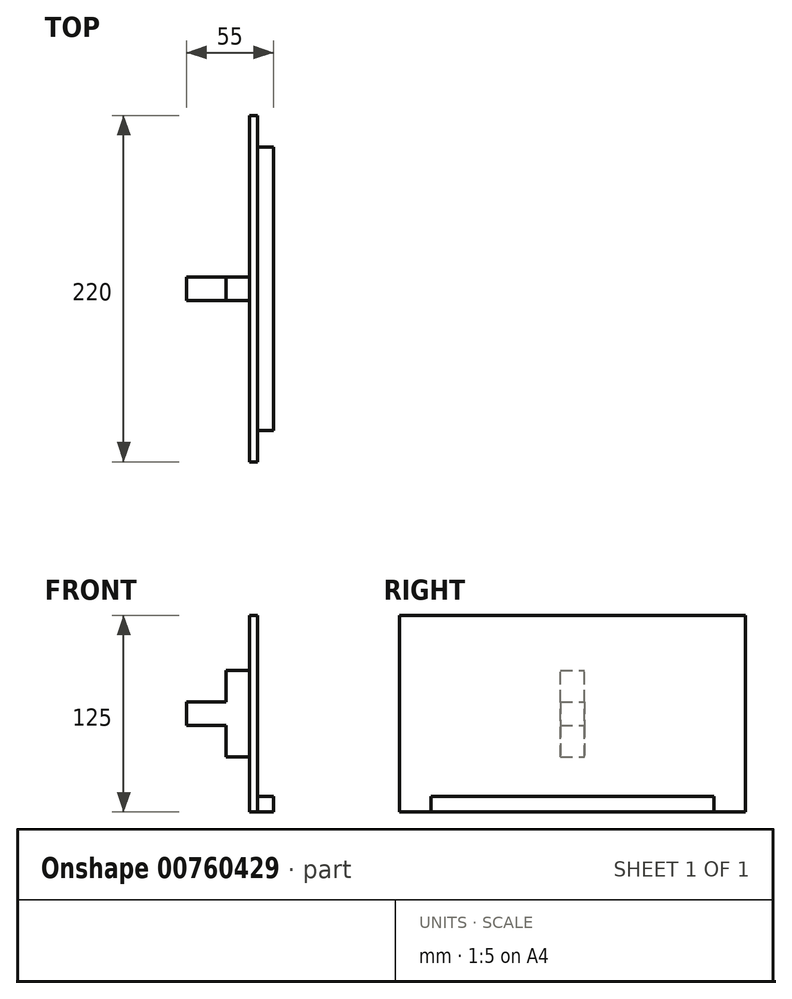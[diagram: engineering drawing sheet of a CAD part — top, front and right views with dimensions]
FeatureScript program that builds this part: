
annotation { "Feature Type Name" : "Feature", "Feature Type Description" : "" }
export const myFeature = defineFeature(function(context is Context, id is Id, definition is map)
    precondition{}
    {
        {
            var Q0;
            Q0=qCreatedBy(makeId("Front.planeOp"),FACE);
            var sketch = newSketch(context, id + "F0", { "sketchPlane" : qUnion([Q0])});
            skLineSegment(sketch, "E0.bottom", {"start": v(-20, 7.5) * mm, "end": v(20, 7.5) * mm});
            skLineSegment(sketch, "E0.top", {"start": v(-20, -7.5) * mm, "end": v(20, -7.5) * mm});
            skLineSegment(sketch, "E0.left", {"start": v(-20, 7.5) * mm, "end": v(-20, -7.5) * mm});
            skLineSegment(sketch, "E0.right", {"start": v(20, 7.5) * mm, "end": v(20, -7.5) * mm});
            skPoint(sketch, "E0.middle", {"position": v(0, 0) * mm});
            skLineSegment(sketch, "E1.bottom", {"start": v(20, 7.5) * mm, "end": v(5, 7.5) * mm});
            skLineSegment(sketch, "E1.top", {"start": v(20, 27.5) * mm, "end": v(5, 27.5) * mm});
            skLineSegment(sketch, "E1.left", {"start": v(20, 7.5) * mm, "end": v(20, 27.5) * mm});
            skLineSegment(sketch, "E1.right", {"start": v(5, 7.5) * mm, "end": v(5, 27.5) * mm});
            skLineSegment(sketch, "E2.bottom", {"start": v(20, -7.5) * mm, "end": v(5, -7.5) * mm});
            skLineSegment(sketch, "E2.top", {"start": v(20, -27.5) * mm, "end": v(5, -27.5) * mm});
            skLineSegment(sketch, "E2.left", {"start": v(20, -7.5) * mm, "end": v(20, -27.5) * mm});
            skLineSegment(sketch, "E2.right", {"start": v(5, -7.5) * mm, "end": v(5, -27.5) * mm});
            skSolve(sketch);
        }
        {
            var Q0;
            Q0=makeQuery(id+"F0.imprint","IMPRINT",FACE,{"disambiguationData":[TD([[makeQuery(id+"F0.imprint","IMPRINT",EDGE,{"derivedFrom":sQuery(id+"F0.wireOp",EDGE,"E1.top")}),1.0]])]});
            var Q1;
            Q1=makeQuery(id+"F0.imprint","IMPRINT",FACE,{"disambiguationData":[TD([[makeQuery(id+"F0.imprint","IMPRINT",EDGE,{"derivedFrom":sQuery(id+"F0.wireOp",EDGE,"E2.top")}),-1.0]])]});
            var Q2;
            {var subQ3=sQuery(id+"F0.wireOp",EDGE,"E0.left");Q2=makeQuery(id+"F0.imprint","IMPRINT",FACE,{"disambiguationData":[TD([[makeQuery(id+"F0.imprint","IMPRINT",EDGE,{"derivedFrom":subQ3}),1.0]])]});}
            extrude(context, id + "F1", {"entities" : qUnion([Q0, Q1, Q2]), "depth" : 15 * mm, "offsetDistance" : 25 * mm});
        }
        {
            var Q0;
            Q0=makeQuery(id+"F1.opExtrude","SWEPT_FACE",FACE,{"disambiguationData":[OSD([sQuery(id+"F0.wireOp",EDGE,"E0.right"),sQuery(id+"F0.wireOp",EDGE,"E1.left"),sQuery(id+"F0.wireOp",EDGE,"E2.left")])]});
            var sketch = newSketch(context, id + "F2", { "sketchPlane" : qUnion([Q0])});
            skLineSegment(sketch, "E3.bottom", {"start": v(102.5, -62.5) * mm, "end": v(-117.5, -62.5) * mm});
            skLineSegment(sketch, "E3.top", {"start": v(102.5, 62.5) * mm, "end": v(-117.5, 62.5) * mm});
            skLineSegment(sketch, "E3.left", {"start": v(102.5, -62.5) * mm, "end": v(102.5, 62.5) * mm});
            skLineSegment(sketch, "E3.right", {"start": v(-117.5, -62.5) * mm, "end": v(-117.5, 62.5) * mm});
            skPoint(sketch, "E3.middle", {"position": v(-7.5, 0) * mm});
            skPoint(sketch, "E3.middle.positionSnap0", {"position": v(-7.5, 27.5) * mm});
            skPoint(sketch, "E3.middle.positionSnap1", {"position": v(-15, 0) * mm});
            skPoint(sketch, "E3.centerSnap0", {"position": v(-7.5, 27.5) * mm});
            skPoint(sketch, "E3.centerSnap1", {"position": v(-15, 0) * mm});
            skSolve(sketch);
        }
        {
            var Q0;
            Q0=makeQuery(id+"F2.imprint","IMPRINT",FACE,{"disambiguationData":[TD([[makeQuery(id+"F2.imprint","IMPRINT",EDGE,{"derivedFrom":sQuery(id+"F2.wireOp",EDGE,"E3.bottom")}),-1.0]])]});
            var Q1;
            {var subQ0=sQuery(id+"F0.wireOp",EDGE,"E1.left");Q1=makeQuery(id+"F2.imprint","IMPRINT",FACE,{"disambiguationData":[TD([[makeQuery(id+"F2.imprint","IMPRINT",EDGE,{"derivedFrom":makeQuery(id+"F1.opExtrude","SWEPT_EDGE",EDGE,{"disambiguationData":[OSD([sQuery(id+"F0.wireOp",EDGE,"E1.top"),subQ0])]})}),-1.0]])]});}
            extrude(context, id + "F3", {"entities" : qUnion([Q0, Q1]), "operationType" : NewBodyOperationType.ADD, "depth" : 5 * mm, "offsetDistance" : 25 * mm});
        }
        {
            var Q0;
            Q0=makeQuery(id+"F3.opExtrude","CAP_FACE",FACE,{"disambiguationData":[OSD([sQuery(id+"F2.wireOp",EDGE,"E3.bottom"),sQuery(id+"F2.wireOp",EDGE,"E3.top"),sQuery(id+"F2.wireOp",EDGE,"E3.left"),sQuery(id+"F2.wireOp",EDGE,"E3.right")])],"isStart":false});
            var sketch = newSketch(context, id + "F4", { "sketchPlane" : qUnion([Q0])});
            skLineSegment(sketch, "E4.bottom", {"start": v(82.5, -62.5) * mm, "end": v(-97.5, -62.5) * mm});
            skLineSegment(sketch, "E4.top", {"start": v(82.5, -52.5) * mm, "end": v(-97.5, -52.5) * mm});
            skLineSegment(sketch, "E4.left", {"start": v(82.5, -62.5) * mm, "end": v(82.5, -52.5) * mm});
            skLineSegment(sketch, "E4.right", {"start": v(-97.5, -62.5) * mm, "end": v(-97.5, -52.5) * mm});
            skPoint(sketch, "E4.middle", {"position": v(-7.5, -57.5) * mm});
            skPoint(sketch, "E4.middle.positionSnap0", {"position": v(-7.5, -62.5) * mm});
            skPoint(sketch, "E4.centerSnap0", {"position": v(-7.5, -62.5) * mm});
            skSolve(sketch);
        }
        {
            var Q0;
            Q0=makeQuery(id+"F4.imprint","IMPRINT",FACE,{"disambiguationData":[TD([[makeQuery(id+"F4.imprint","IMPRINT",EDGE,{"derivedFrom":sQuery(id+"F4.wireOp",EDGE,"E4.bottom")}),-1.0]])]});
            extrude(context, id + "F5", {"entities" : qUnion([Q0]), "operationType" : NewBodyOperationType.ADD, "depth" : 10 * mm, "offsetDistance" : 25 * mm});
        }
    });
